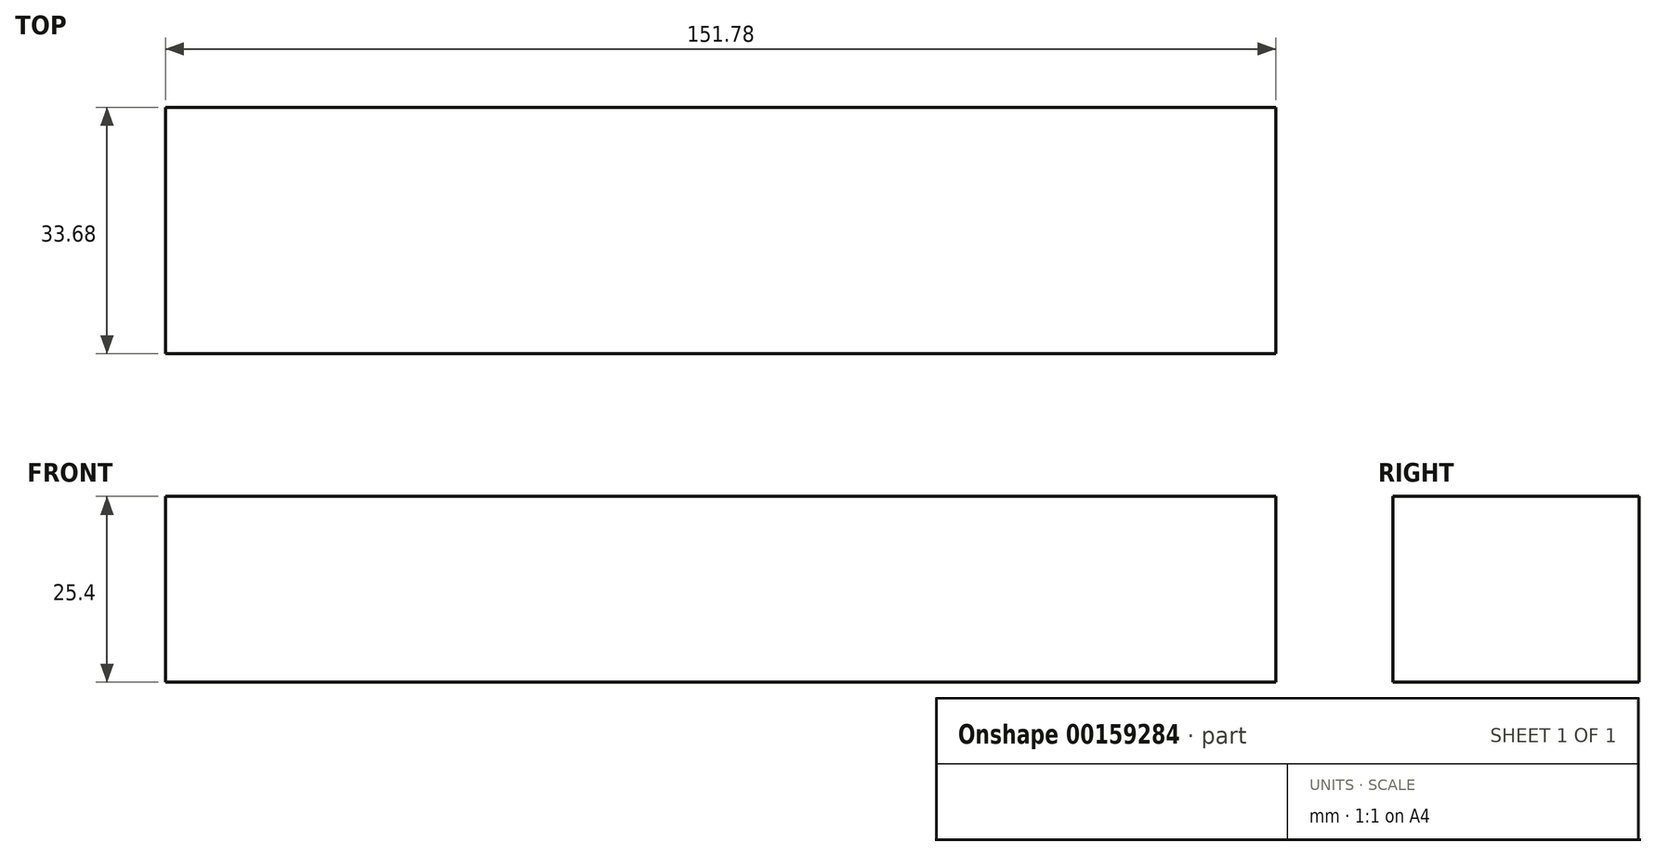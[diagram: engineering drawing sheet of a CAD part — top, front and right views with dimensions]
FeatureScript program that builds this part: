
annotation { "Feature Type Name" : "Feature", "Feature Type Description" : "" }
export const myFeature = defineFeature(function(context is Context, id is Id, definition is map)
    precondition{}
    {
        {
            var Q0;
            Q0=qCreatedBy(makeId("Top.planeOp"),FACE);
            var sketch = newSketch(context, id + "F0", { "sketchPlane" : qUnion([Q0])});
            skLineSegment(sketch, "E0.bottom", {"start": v(-104.54, -17.75) * mm, "end": v(47.24, -17.75) * mm});
            skLineSegment(sketch, "E0.top", {"start": v(-104.54, -51.43) * mm, "end": v(47.24, -51.43) * mm});
            skLineSegment(sketch, "E0.left", {"start": v(-104.54, -17.75) * mm, "end": v(-104.54, -51.43) * mm});
            skLineSegment(sketch, "E0.right", {"start": v(47.24, -17.75) * mm, "end": v(47.24, -51.43) * mm});
            skSolve(sketch);
        }
        {
            var Q0;
            Q0=makeQuery(id+"F0.imprint","IMPRINT",FACE,{"disambiguationData":[TD([[makeQuery(id+"F0.imprint","IMPRINT",EDGE,{"derivedFrom":sQuery(id+"F0.wireOp",EDGE,"E0.bottom")}),-1.0]])]});
            extrude(context, id + "F1", {"entities" : qUnion([Q0]), "depth" : 25.4 * mm});
        }
    });
